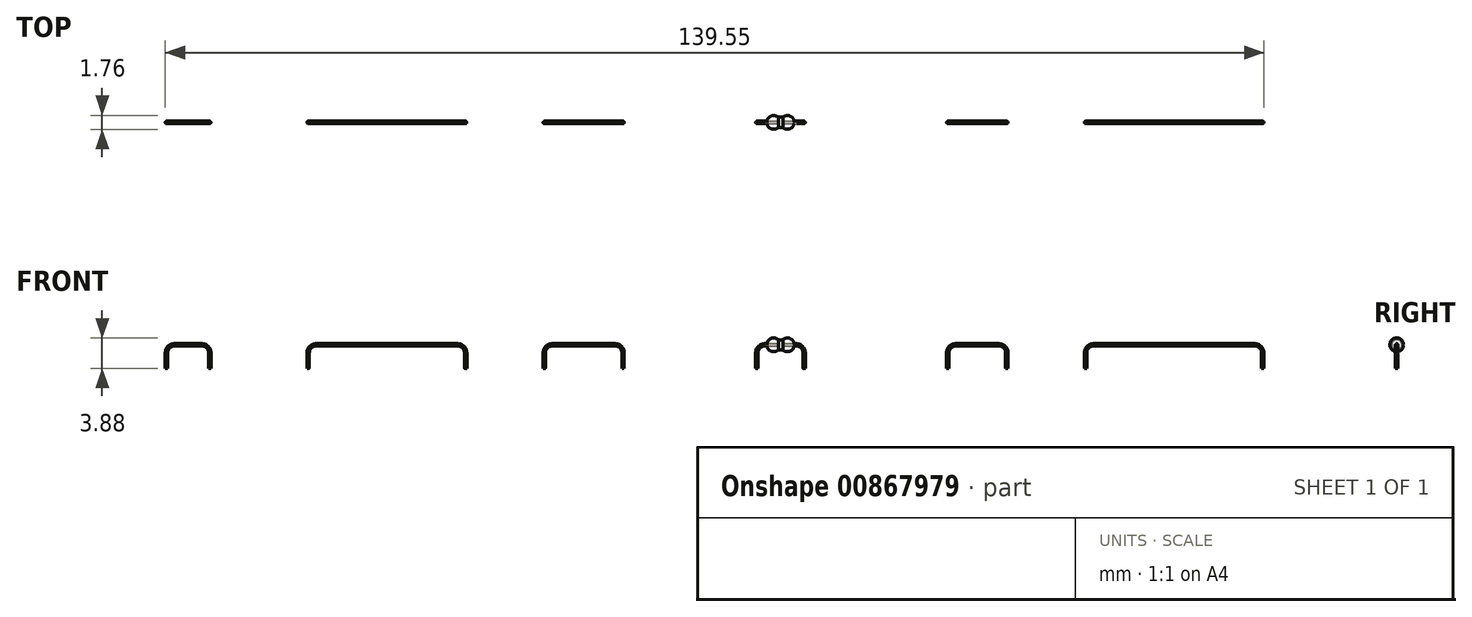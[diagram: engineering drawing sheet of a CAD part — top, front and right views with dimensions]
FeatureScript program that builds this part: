
annotation { "Feature Type Name" : "Feature", "Feature Type Description" : "" }
export const myFeature = defineFeature(function(context is Context, id is Id, definition is map)
    precondition{}
    {
        {
            var Q0;
            Q0=qCreatedBy(makeId("Front.planeOp"),FACE);
            var sketch = newSketch(context, id + "F0", { "sketchPlane" : qUnion([Q0])});
            skLineSegment(sketch, "E0.bottom", {"start": v(0.88, -0.65) * mm, "end": v(-0.88, -0.65) * mm});
            skLineSegment(sketch, "E0.top", {"start": v(0.88, 0.65) * mm, "end": v(-0.88, 0.65) * mm});
            skLineSegment(sketch, "E0.left", {"start": v(0.88, -0.65) * mm, "end": v(0.88, 0.65) * mm});
            skLineSegment(sketch, "E0.right", {"start": v(-0.87, -0.65) * mm, "end": v(-0.87, 0.65) * mm});
            skPoint(sketch, "E0.middle", {"position": v(0, 0) * mm});
            skCircle(sketch, "E1", {"center": v(0.88, 0) * mm, "radius": 0.88 * mm});
            skCircle(sketch, "E2", {"center": v(-0.88, 0) * mm, "radius": 0.88 * mm});
            skLineSegment(sketch, "E3", {"start": v(-1.75, 0) * mm, "end": v(1.75, 0) * mm});
            skSolve(sketch);
        }
        {
            var Q0;
            {var subQ0=sQuery(id+"F0.wireOp",EDGE,"E0.right");var subQ1=sQuery(id+"F0.wireOp",EDGE,"E0.top");var subQ2=makeQuery(id+"F0.imprint","INTERSECT",VERTEX,{"derivedFrom":[subQ1,subQ0]});Q0=makeQuery(id+"F0.imprint","IMPRINT",FACE,{"disambiguationData":[TD([[makeQuery(id+"F0.imprint","IMPRINT",EDGE,{"disambiguationData":[TD([[subQ2,1.0]])],"derivedFrom":subQ1}),-1.0]])]});}
            var Q1;
            {var subQ0=sQuery(id+"F0.wireOp",EDGE,"E0.right");var subQ1=sQuery(id+"F0.wireOp",EDGE,"E0.top");var subQ2=makeQuery(id+"F0.imprint","INTERSECT",VERTEX,{"derivedFrom":[subQ1,subQ0]});Q1=makeQuery(id+"F0.imprint","IMPRINT",FACE,{"disambiguationData":[TD([[makeQuery(id+"F0.imprint","IMPRINT",EDGE,{"disambiguationData":[TD([[subQ2,1.0]])],"derivedFrom":subQ1}),1.0]])]});}
            var Q2;
            {var subQ0=sQuery(id+"F0.wireOp",EDGE,"E0.left");var subQ1=sQuery(id+"F0.wireOp",EDGE,"E0.top");var subQ2=makeQuery(id+"F0.imprint","INTERSECT",VERTEX,{"derivedFrom":[subQ1,subQ0]});Q2=makeQuery(id+"F0.imprint","IMPRINT",FACE,{"disambiguationData":[TD([[makeQuery(id+"F0.imprint","IMPRINT",EDGE,{"disambiguationData":[TD([[subQ2,-1.0]])],"derivedFrom":subQ1}),1.0]])]});}
            var Q3;
            {var subQ0=sQuery(id+"F0.wireOp",EDGE,"E0.left");var subQ1=sQuery(id+"F0.wireOp",EDGE,"E0.top");var subQ2=makeQuery(id+"F0.imprint","INTERSECT",VERTEX,{"derivedFrom":[subQ1,subQ0]});Q3=makeQuery(id+"F0.imprint","IMPRINT",FACE,{"disambiguationData":[TD([[makeQuery(id+"F0.imprint","IMPRINT",EDGE,{"disambiguationData":[TD([[subQ2,-1.0]])],"derivedFrom":subQ1}),-1.0]])]});}
            var Q4;
            {var subQ0=sQuery(id+"F0.wireOp",EDGE,"E1");var subQ1=sQuery(id+"F0.wireOp",EDGE,"E0.top");var subQ2=makeQuery(id+"F0.imprint","INTERSECT",VERTEX,{"derivedFrom":[subQ1,subQ0]});Q4=makeQuery(id+"F0.imprint","IMPRINT",FACE,{"disambiguationData":[TD([[makeQuery(id+"F0.imprint","IMPRINT",EDGE,{"disambiguationData":[TD([[subQ2,-1.0]])],"derivedFrom":subQ1}),1.0]])]});}
            var Q5;
            Q5=sQuery(id+"F0.wireOp",EDGE,"E0.top");
            var Q6;
            Q6=sQuery(id+"F0.wireOp",EDGE,"E1");
            var Q7;
            Q7=sQuery(id+"F0.wireOp",EDGE,"E2");
            var Q8;
            Q8=sQuery(id+"F0.wireOp",EDGE,"E3");
            revolve(context, id + "F1", {"surfaceOperationType" : NewSurfaceOperationType.NEW, "entities" : qUnion([Q0, Q1, Q2, Q3, Q4]), "surfaceEntities" : qUnion([Q5, Q6, Q7]), "axis" : qUnion([Q8]), "revolveType" : RevolveType.FULL});
        }
        {
            var Q0;
            Q0=qCreatedBy(makeId("Front.planeOp"),FACE);
            var sketch = newSketch(context, id + "F2", { "sketchPlane" : qUnion([Q0])});
            skLineSegment(sketch, "E4", {"start": v(0, 0) * mm, "end": v(-2, 0) * mm});
            skLineSegment(sketch, "E5", {"start": v(0, 0) * mm, "end": v(2, 0) * mm});
            skArc(sketch, "E6", {"start": v(-2, 0) * mm, "mid": v(-2.7, -0.3) * mm, "end": v(-3, -1) * mm});
            skArc(sketch, "E7", {"start": v(3, -1) * mm, "mid": v(2.7, -0.3) * mm, "end": v(2, 0) * mm});
            skLineSegment(sketch, "E8", {"start": v(-3, -1) * mm, "end": v(-3, -3) * mm});
            skLineSegment(sketch, "E9", {"start": v(3, -1) * mm, "end": v(3, -3) * mm});
            skSolve(sketch);
        }
        {
            var Q0;
            Q0=qCreatedBy(makeId("Right.planeOp"),FACE);
            var sketch = newSketch(context, id + "F3", { "sketchPlane" : qUnion([Q0])});
            skCircle(sketch, "E10", {"center": v(0, 0) * mm, "radius": 0.15 * mm});
            skSolve(sketch);
        }
        {
            var Q0;
            Q0 = qSketchRegion(id + "F3", true);
            var Q1;
            Q1 = qConstructionFilter(qBodyType(qCreatedBy(id + "F2" ,EDGE), BodyType.WIRE), ConstructionObject.NO);
            sweep(context, id + "F4", {"profiles" : qUnion([Q0]), "path" : qUnion([Q1])});
        }
        {
            var Q0;
            Q0=qCreatedBy(makeId("Right.planeOp"),FACE);
            cPlane(context, id + "F5", {"entities" : qUnion([Q0]), "cplaneType" : CPlaneType.OFFSET, "offset" : 25 * mm, "width" : 150 * mm, "height" : 150 * mm});
        }
        {
            var Q0;
            Q0=qCreatedBy(id+"F5.planeOp",FACE);
            cPlane(context, id + "F6", {"entities" : qUnion([Q0]), "cplaneType" : CPlaneType.OFFSET, "offset" : 25 * mm, "width" : 150 * mm, "height" : 150 * mm});
        }
        {
            var Q0;
            Q0=qCreatedBy(makeId("Front.planeOp"),FACE);
            var sketch = newSketch(context, id + "F7", { "sketchPlane" : qUnion([Q0])});
            skLineSegment(sketch, "E11", {"start": v(25, 0) * mm, "end": v(22.25, 0) * mm});
            skLineSegment(sketch, "E12", {"start": v(25, 0) * mm, "end": v(27.75, 0) * mm});
            skArc(sketch, "E13", {"start": v(22.25, 0) * mm, "mid": v(21.54, -0.3) * mm, "end": v(21.25, -1) * mm});
            skArc(sketch, "E14", {"start": v(28.75, -1) * mm, "mid": v(28.46, -0.3) * mm, "end": v(27.75, 0) * mm});
            skLineSegment(sketch, "E15", {"start": v(21.25, -1) * mm, "end": v(21.25, -3) * mm});
            skLineSegment(sketch, "E16", {"start": v(28.75, -1) * mm, "end": v(28.75, -3) * mm});
            skSolve(sketch);
        }
        {
            var Q0;
            Q0=qCreatedBy(makeId("Front.planeOp"),FACE);
            var sketch = newSketch(context, id + "F8", { "sketchPlane" : qUnion([Q0])});
            skLineSegment(sketch, "E17", {"start": v(50, 0) * mm, "end": v(39.75, 0) * mm});
            skLineSegment(sketch, "E18", {"start": v(50, 0) * mm, "end": v(60.25, 0) * mm});
            skArc(sketch, "E19", {"start": v(39.75, 0) * mm, "mid": v(39.04, -0.3) * mm, "end": v(38.75, -1) * mm});
            skArc(sketch, "E20", {"start": v(61.25, -1) * mm, "mid": v(60.96, -0.3) * mm, "end": v(60.25, 0) * mm});
            skLineSegment(sketch, "E21", {"start": v(38.75, -1) * mm, "end": v(38.75, -3) * mm});
            skLineSegment(sketch, "E22", {"start": v(61.25, -1) * mm, "end": v(61.25, -3) * mm});
            skSolve(sketch);
        }
        {
            var Q0;
            Q0=qCreatedBy(id+"F5.planeOp",FACE);
            var sketch = newSketch(context, id + "F9", { "sketchPlane" : qUnion([Q0])});
            skCircle(sketch, "E23", {"center": v(0, 0) * mm, "radius": 0.15 * mm});
            skSolve(sketch);
        }
        {
            var Q0;
            Q0=qCreatedBy(id+"F6.planeOp",FACE);
            var sketch = newSketch(context, id + "F10", { "sketchPlane" : qUnion([Q0])});
            skCircle(sketch, "E24", {"center": v(0, 0) * mm, "radius": 0.15 * mm});
            skSolve(sketch);
        }
        {
            var Q0;
            Q0=makeQuery(id+"F9.imprint","IMPRINT",FACE,{"disambiguationData":[TD([[makeQuery(id+"F9.imprint","IMPRINT",EDGE,{"derivedFrom":sQuery(id+"F9.wireOp",EDGE,"E23")}),1.0]])]});
            var Q1;
            Q1=sQuery(id+"F7.wireOp",EDGE,"E12");
            var Q2;
            Q2=sQuery(id+"F7.wireOp",EDGE,"E14");
            var Q3;
            Q3=sQuery(id+"F7.wireOp",EDGE,"E16");
            var Q4;
            Q4=sQuery(id+"F7.wireOp",EDGE,"E11");
            var Q5;
            Q5=sQuery(id+"F7.wireOp",EDGE,"E13");
            var Q6;
            Q6=sQuery(id+"F7.wireOp",EDGE,"E15");
            sweep(context, id + "F11", {"profiles" : qUnion([Q0]), "path" : qUnion([Q1, Q2, Q3, Q4, Q5, Q6])});
        }
        {
            var Q0;
            Q0=makeQuery(id+"F10.imprint","IMPRINT",FACE,{"disambiguationData":[TD([[makeQuery(id+"F10.imprint","IMPRINT",EDGE,{"derivedFrom":sQuery(id+"F10.wireOp",EDGE,"E24")}),1.0]])]});
            var Q1;
            Q1=sQuery(id+"F8.wireOp",EDGE,"E18");
            var Q2;
            Q2=sQuery(id+"F8.wireOp",EDGE,"E20");
            var Q3;
            Q3=sQuery(id+"F8.wireOp",EDGE,"E22");
            var Q4;
            Q4=sQuery(id+"F8.wireOp",EDGE,"E17");
            var Q5;
            Q5=sQuery(id+"F8.wireOp",EDGE,"E19");
            var Q6;
            Q6=sQuery(id+"F8.wireOp",EDGE,"E21");
            sweep(context, id + "F12", {"profiles" : qUnion([Q0]), "path" : qUnion([Q1, Q2, Q3, Q4, Q5, Q6])});
        }
        {
            var Q0;
            Q0=qCreatedBy(makeId("Right.planeOp"),FACE);
            cPlane(context, id + "F13", {"entities" : qUnion([Q0]), "cplaneType" : CPlaneType.OFFSET, "offset" : 25 * mm, "oppositeDirection" : true, "width" : 150 * mm, "height" : 150 * mm});
        }
        {
            var Q0;
            Q0=qCreatedBy(id+"F13.planeOp",FACE);
            cPlane(context, id + "F14", {"entities" : qUnion([Q0]), "cplaneType" : CPlaneType.OFFSET, "offset" : 25 * mm, "oppositeDirection" : true, "width" : 150 * mm, "height" : 150 * mm});
        }
        {
            var Q0;
            Q0=qCreatedBy(makeId("Front.planeOp"),FACE);
            var sketch = newSketch(context, id + "F15", { "sketchPlane" : qUnion([Q0])});
            skLineSegment(sketch, "E25", {"start": v(-25, 0) * mm, "end": v(-29, 0) * mm});
            skLineSegment(sketch, "E26", {"start": v(-25, 0) * mm, "end": v(-21, 0) * mm});
            skArc(sketch, "E27", {"start": v(-29, 0) * mm, "mid": v(-29.7, -0.3) * mm, "end": v(-30, -1) * mm});
            skArc(sketch, "E28", {"start": v(-20, -1) * mm, "mid": v(-20.3, -0.3) * mm, "end": v(-21, 0) * mm});
            skLineSegment(sketch, "E29", {"start": v(-30, -1) * mm, "end": v(-30, -3) * mm});
            skLineSegment(sketch, "E30", {"start": v(-20, -1) * mm, "end": v(-20, -3) * mm});
            skSolve(sketch);
        }
        {
            var Q0;
            Q0=qCreatedBy(makeId("Front.planeOp"),FACE);
            var sketch = newSketch(context, id + "F16", { "sketchPlane" : qUnion([Q0])});
            skLineSegment(sketch, "E31", {"start": v(-50, 0) * mm, "end": v(-59, 0) * mm});
            skLineSegment(sketch, "E32", {"start": v(-50, 0) * mm, "end": v(-41, 0) * mm});
            skArc(sketch, "E33", {"start": v(-59, 0) * mm, "mid": v(-59.7, -0.3) * mm, "end": v(-60, -1) * mm});
            skArc(sketch, "E34", {"start": v(-40, -1) * mm, "mid": v(-40.3, -0.3) * mm, "end": v(-41, 0) * mm});
            skLineSegment(sketch, "E35", {"start": v(-60, -1) * mm, "end": v(-60, -3) * mm});
            skLineSegment(sketch, "E36", {"start": v(-40, -1) * mm, "end": v(-40, -3) * mm});
            skSolve(sketch);
        }
        {
            var Q0;
            Q0=qCreatedBy(id+"F13.planeOp",FACE);
            var sketch = newSketch(context, id + "F17", { "sketchPlane" : qUnion([Q0])});
            skCircle(sketch, "E37", {"center": v(0, 0) * mm, "radius": 0.15 * mm});
            skSolve(sketch);
        }
        {
            var Q0;
            Q0=qCreatedBy(id+"F14.planeOp",FACE);
            var sketch = newSketch(context, id + "F18", { "sketchPlane" : qUnion([Q0])});
            skCircle(sketch, "E38", {"center": v(0, 0) * mm, "radius": 0.15 * mm});
            skSolve(sketch);
        }
        {
            var Q0;
            Q0=makeQuery(id+"F17.imprint","IMPRINT",FACE,{"disambiguationData":[TD([[makeQuery(id+"F17.imprint","IMPRINT",EDGE,{"derivedFrom":sQuery(id+"F17.wireOp",EDGE,"E37")}),1.0]])]});
            var Q1;
            Q1=sQuery(id+"F15.wireOp",EDGE,"E26");
            var Q2;
            Q2=sQuery(id+"F15.wireOp",EDGE,"E28");
            var Q3;
            Q3=sQuery(id+"F15.wireOp",EDGE,"E30");
            var Q4;
            Q4=sQuery(id+"F15.wireOp",EDGE,"E25");
            var Q5;
            Q5=sQuery(id+"F15.wireOp",EDGE,"E27");
            var Q6;
            Q6=sQuery(id+"F15.wireOp",EDGE,"E29");
            sweep(context, id + "F19", {"profiles" : qUnion([Q0]), "path" : qUnion([Q1, Q2, Q3, Q4, Q5, Q6])});
        }
        {
            var Q0;
            Q0=makeQuery(id+"F18.imprint","IMPRINT",FACE,{"disambiguationData":[TD([[makeQuery(id+"F18.imprint","IMPRINT",EDGE,{"derivedFrom":sQuery(id+"F18.wireOp",EDGE,"E38")}),1.0]])]});
            var Q1;
            Q1=sQuery(id+"F16.wireOp",EDGE,"E32");
            var Q2;
            Q2=sQuery(id+"F16.wireOp",EDGE,"E34");
            var Q3;
            Q3=sQuery(id+"F16.wireOp",EDGE,"E31");
            var Q4;
            Q4=sQuery(id+"F16.wireOp",EDGE,"E36");
            var Q5;
            Q5=sQuery(id+"F16.wireOp",EDGE,"E33");
            var Q6;
            Q6=sQuery(id+"F16.wireOp",EDGE,"E35");
            sweep(context, id + "F20", {"profiles" : qUnion([Q0]), "path" : qUnion([Q1, Q2, Q3, Q4, Q5, Q6])});
        }
        {
            var Q0;
            Q0=qCreatedBy(id+"F14.planeOp",FACE);
            cPlane(context, id + "F21", {"entities" : qUnion([Q0]), "cplaneType" : CPlaneType.OFFSET, "offset" : 25 * mm, "oppositeDirection" : true, "width" : 150 * mm, "height" : 150 * mm});
        }
        {
            var Q0;
            Q0=qCreatedBy(makeId("Front.planeOp"),FACE);
            var sketch = newSketch(context, id + "F22", { "sketchPlane" : qUnion([Q0])});
            skLineSegment(sketch, "E39", {"start": v(-75, 0) * mm, "end": v(-77, 0) * mm});
            skLineSegment(sketch, "E40", {"start": v(-75, 0) * mm, "end": v(-73.5, 0) * mm});
            skArc(sketch, "E41", {"start": v(-77, 0) * mm, "mid": v(-77.7, -0.3) * mm, "end": v(-78, -1) * mm});
            skArc(sketch, "E42", {"start": v(-72.5, -1) * mm, "mid": v(-72.8, -0.3) * mm, "end": v(-73.5, 0) * mm});
            skLineSegment(sketch, "E43", {"start": v(-78, -1) * mm, "end": v(-78, -3) * mm});
            skLineSegment(sketch, "E44", {"start": v(-72.5, -1) * mm, "end": v(-72.5, -3) * mm});
            skSolve(sketch);
        }
        {
            var Q0;
            Q0=qCreatedBy(id+"F21.planeOp",FACE);
            var sketch = newSketch(context, id + "F23", { "sketchPlane" : qUnion([Q0])});
            skCircle(sketch, "E45", {"center": v(0, 0) * mm, "radius": 0.15 * mm});
            skSolve(sketch);
        }
        {
            var Q0;
            Q0=makeQuery(id+"F23.imprint","IMPRINT",FACE,{"disambiguationData":[TD([[makeQuery(id+"F23.imprint","IMPRINT",EDGE,{"derivedFrom":sQuery(id+"F23.wireOp",EDGE,"E45")}),1.0]])]});
            var Q1;
            Q1=sQuery(id+"F22.wireOp",EDGE,"E40");
            var Q2;
            Q2=sQuery(id+"F22.wireOp",EDGE,"E42");
            var Q3;
            Q3=sQuery(id+"F22.wireOp",EDGE,"E44");
            var Q4;
            Q4=sQuery(id+"F22.wireOp",EDGE,"E39");
            var Q5;
            Q5=sQuery(id+"F22.wireOp",EDGE,"E41");
            var Q6;
            Q6=sQuery(id+"F22.wireOp",EDGE,"E43");
            sweep(context, id + "F24", {"profiles" : qUnion([Q0]), "path" : qUnion([Q1, Q2, Q3, Q4, Q5, Q6])});
        }
    });
